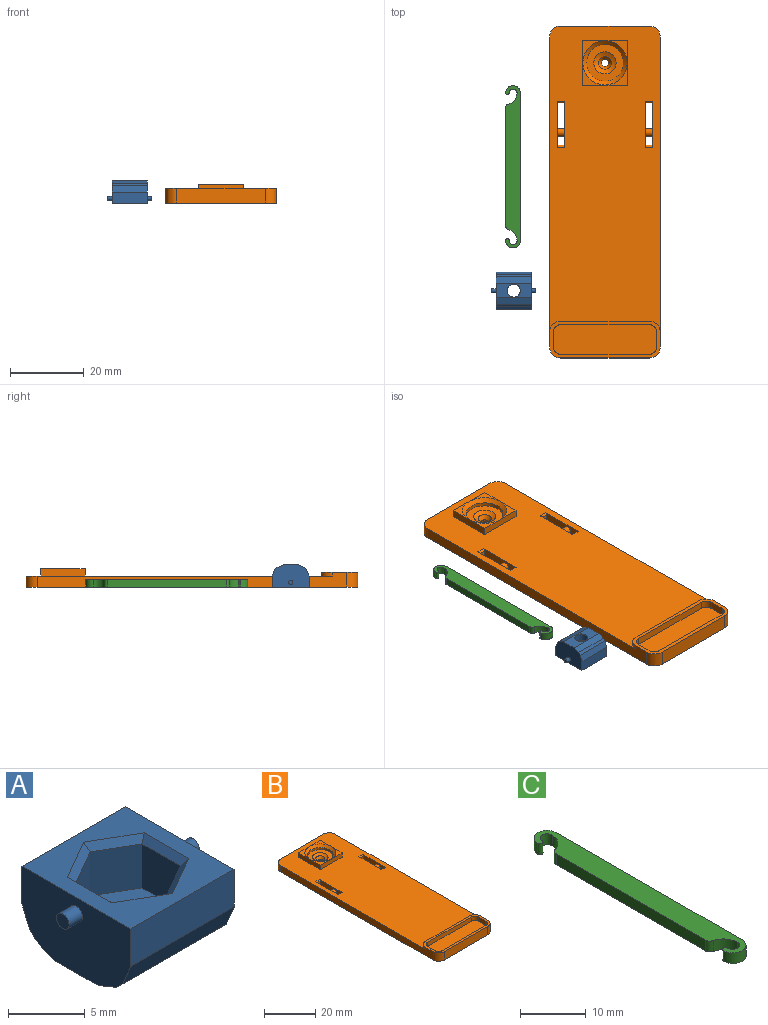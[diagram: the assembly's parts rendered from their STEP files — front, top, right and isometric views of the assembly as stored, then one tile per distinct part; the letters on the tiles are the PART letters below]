
ASSEMBLY  parts=3 mates=2
PART A: 30 faces, bbox 12x10x6 mm
  f0: plane 10x9.5mm, normal (0,0,1), area 51.6mm2, adj f3,f4,f5,f6,f24,f25,f26,f27
  f1: plane 1.15x1.15mm, normal (-1,0,0), area 1mm2, adj f2
  f2: cylinder r=0.57mm len=1.25mm, axis (1,0,0), area 4.5mm2, adj f1,f3
  f3: plane 10x6mm, normal (-1,0,0), area 53.5mm2, adj f0,f2,f4,f6,f7,f10,f11,f19
  f4: plane 9.5x3mm, normal (0,-1,0), area 28.5mm2, adj f0,f3,f5,f22
  f5: plane 10x6mm, normal (1,0,0), area 53.5mm2, adj f0,f4,f6,f7,f9,f10,f11,f19
  f6: plane 9.5x3mm, normal (0,1,0), area 28.5mm2, adj f0,f3,f5,f19
  f7: plane 9.5x4mm, normal (0,0,-1), area 28.4mm2, adj f3,f5,f20,f21,f23
  f8: plane 1.15x1.15mm, normal (1,0,0), area 1mm2, adj f9
  f9: cylinder r=0.57mm len=1.25mm, axis (1,0,0), area 4.5mm2, adj f5,f8
  f10: plane 9.5x0.59mm, normal (0,0.71,-0.71), area 7.9mm2, adj f3,f5,f19,f20
  f11: plane 9.5x0.59mm, normal (0,-0.71,-0.71), area 7.9mm2, adj f3,f5,f21,f22
  f12: plane 3.5x3.04mm, normal (-0.5,-0.87,0), area 12.3mm2, adj f13,f17,f18,f26
  f13: plane 3.5x3.04mm, normal (0.5,-0.87,0), area 12.3mm2, adj f12,f14,f18,f28
  f14: plane 3.51x3.5mm, normal (1,0,0), area 12.3mm2, adj f13,f15,f18,f29
  f15: plane 3.5x3.04mm, normal (0.5,0.87,0), area 12.3mm2, adj f14,f16,f18,f27
  f16: plane 3.5x3.04mm, normal (-0.5,0.87,0), area 12.3mm2, adj f15,f17,f18,f25
  f17: plane 3.51x3.5mm, normal (-1,0,0), area 12.3mm2, adj f12,f16,f18,f24
  f18: plane 7.02x6.08mm, normal (0,0,1), area 22.4mm2, adj f12,f13,f14,f15,f16,f17,f23
  f19: plane 9.5x1.71mm, normal (0,0.92,-0.38), area 17.6mm2, adj f3,f5,f6,f10
  f20: plane 9.5x1.71mm, normal (0,0.38,-0.92), area 17.6mm2, adj f3,f5,f7,f10
  f21: plane 9.5x1.71mm, normal (0,-0.38,-0.92), area 17.6mm2, adj f3,f5,f7,f11
  f22: plane 9.5x1.71mm, normal (0,-0.92,-0.38), area 17.6mm2, adj f3,f4,f5,f11
  f23: cylinder r=1.75mm len=3.5mm, axis (0,0,1), area 22mm2, adj f7,f18
  f24: plane 4.09x0.5mm, normal (-0.71,0,0.71), area 2.7mm2, adj f0,f17,f25,f26
  f25: plane 3.54x2.33mm, normal (-0.35,0.61,0.71), area 2.7mm2, adj f0,f16,f24,f27
  f26: plane 3.54x2.33mm, normal (-0.35,-0.61,0.71), area 2.7mm2, adj f0,f12,f24,f28
  f27: plane 3.54x2.33mm, normal (0.35,0.61,0.71), area 2.7mm2, adj f0,f15,f25,f29
  f28: plane 3.54x2.33mm, normal (0.35,-0.61,0.71), area 2.7mm2, adj f0,f13,f26,f29
  f29: plane 4.09x0.5mm, normal (0.71,0,0.71), area 2.7mm2, adj f0,f14,f27,f28
PART B: 56 faces, bbox 30x90x5 mm
  f0: plane 83x30mm, normal (0,0,1), area 2202.2mm2, adj f6,f8,f9,f12,f13,f14,f15,f16
  f1: plane 90x30mm, normal (0,0,-1), area 2631.5mm2, adj f6,f7,f8,f9,f10,f11,f12,f13
  f2: sphere r=5mm, area 21mm2, adj f32,f36
  f3: plane 6x6mm, normal (0,0,1), area 7.7mm2, adj f29,f30,f34
  f4: plane 6x6mm, normal (0,0,1), area 7.7mm2, adj f28,f29,f34
  f5: plane 6x6mm, normal (0,0,1), area 7.7mm2, adj f27,f28,f34
  f6: plane 84x4mm, normal (-1,0,0), area 256mm2, adj f0,f1,f10,f13,f16,f25
  f7: plane 24x4mm, normal (0,-1,0), area 96mm2, adj f1,f10,f11,f25
  f8: plane 84x4mm, normal (1,0,0), area 256mm2, adj f0,f1,f11,f12,f14,f25
  f9: plane 24x3mm, normal (0,1,0), area 72mm2, adj f0,f1,f12,f13
  f10: cylinder r=3mm len=4mm, axis (0,0,-1), area 18.8mm2, adj f1,f6,f7,f25
  f11: cylinder r=3mm len=4mm, axis (0,0,1), area 18.8mm2, adj f1,f7,f8,f25
  f12: cylinder r=3mm len=3mm, axis (0,0,-1), area 14.1mm2, adj f0,f1,f8,f9
  f13: cylinder r=3mm len=3mm, axis (0,0,1), area 14.1mm2, adj f0,f1,f6,f9
  f14: cylinder r=3mm len=3mm, axis (0,0,-1), area 4.7mm2, adj f0,f8,f15,f25
  f15: plane 24x1mm, normal (0,1,0), area 24mm2, adj f0,f14,f16,f25
  f16: cylinder r=3mm len=3mm, axis (0,0,-1), area 4.7mm2, adj f0,f6,f15,f25
  f17: plane 4x2mm, normal (-1,0,0), area 8mm2, adj f18,f24,f25,f26
  f18: cylinder r=2mm len=2mm, axis (0,0,-1), area 6.3mm2, adj f17,f19,f25,f26
  f19: plane 24x2mm, normal (0,1,0), area 48mm2, adj f18,f20,f25,f26
  f20: cylinder r=2mm len=2mm, axis (0,0,-1), area 6.3mm2, adj f19,f21,f25,f26
  f21: plane 4x2mm, normal (1,0,0), area 8mm2, adj f20,f22,f25,f26
  f22: cylinder r=2mm len=2mm, axis (0,0,-1), area 6.3mm2, adj f21,f23,f25,f26
  f23: plane 24x2mm, normal (0,-1,0), area 48mm2, adj f22,f24,f25,f26
  f24: cylinder r=2mm len=2mm, axis (0,0,-1), area 6.3mm2, adj f17,f23,f25,f26
  f25: plane 30x10mm, normal (0,0,1), area 71.7mm2, adj f6,f7,f8,f10,f11,f14,f15,f16
  f26: plane 28x8mm, normal (0,0,1), area 220.6mm2, adj f17,f18,f19,f20,f21,f22,f23,f24
  f27: plane 12x2mm, normal (0,1,0), area 24mm2, adj f0,f5,f28,f30,f31
  f28: plane 12x2mm, normal (-1,0,0), area 24mm2, adj f0,f4,f5,f27,f29
  f29: plane 12x2mm, normal (0,-1,0), area 24mm2, adj f0,f3,f4,f28,f30
  f30: plane 12x2mm, normal (1,0,0), area 24mm2, adj f0,f3,f27,f29,f31
  f31: plane 6x6mm, normal (0,0,1), area 7.7mm2, adj f27,f30,f34
  f32: plane 10x10mm, normal (0,0,1), area 50.3mm2, adj f2,f33
  f33: cylinder r=5mm len=10mm, axis (0,0,-1), area 31.4mm2, adj f32,f34
  f34: cone r=6mm half-angle=45deg, axis (0,0,1), area 48.9mm2, adj f3,f4,f5,f31,f33
  f35: cylinder r=1mm len=2mm, axis (0,0,1), area 4.3mm2, adj f36,f37
  f36: cone r=1.79mm half-angle=34.5deg, axis (0,0,1), area 12.2mm2, adj f2,f35
  f37: cone r=1mm half-angle=45deg, axis (0,0,-1), area 5.6mm2, adj f1,f35
  f38: plane 2.15x2mm, normal (0,-1,0), area 4.3mm2, adj f39,f40,f52,f53
  f39: plane 12.5x3mm, normal (-1,0,0), area 31.9mm2, adj f0,f1,f38,f41,f47,f52,f53,f54
  f40: plane 12.5x3mm, normal (1,0,0), area 31.9mm2, adj f0,f1,f38,f41,f47,f52,f53,f54
  f41: plane 2.15x2mm, normal (0,1,0), area 4.3mm2, adj f39,f40,f54,f55
  f42: plane 2.15x2mm, normal (0,1,0), area 4.3mm2, adj f43,f45,f49,f50
  f43: plane 12.5x3mm, normal (-1,0,0), area 31.9mm2, adj f0,f1,f42,f44,f46,f48,f49,f50
  f44: plane 2.15x2mm, normal (0,-1,0), area 4.3mm2, adj f43,f45,f48,f51
  f45: plane 12.5x3mm, normal (1,0,0), area 31.9mm2, adj f0,f1,f42,f44,f46,f48,f49,f50
  f46: cylinder r=1mm len=2.15mm, axis (-1,0,0), area 13.5mm2, adj f43,f45
  f47: cylinder r=1mm len=2.15mm, axis (-1,0,0), area 13.5mm2, adj f39,f40
  f48: plane 2.15x0.5mm, normal (0,-0.71,0.71), area 1.5mm2, adj f0,f43,f44,f45
  f49: plane 2.15x0.5mm, normal (0,0.71,0.71), area 1.5mm2, adj f0,f42,f43,f45
  f50: plane 2.15x0.5mm, normal (0,0.71,-0.71), area 1.5mm2, adj f1,f42,f43,f45
  f51: plane 2.15x0.5mm, normal (0,-0.71,-0.71), area 1.5mm2, adj f1,f43,f44,f45
  f52: plane 2.15x0.5mm, normal (0,-0.71,-0.71), area 1.5mm2, adj f1,f38,f39,f40
  f53: plane 2.15x0.5mm, normal (0,-0.71,0.71), area 1.5mm2, adj f0,f38,f39,f40
  f54: plane 2.15x0.5mm, normal (0,0.71,-0.71), area 1.5mm2, adj f1,f39,f40,f41
  f55: plane 2.15x0.5mm, normal (0,0.71,0.71), area 1.5mm2, adj f0,f39,f40,f41
PART C: 14 faces, bbox 4x44x2 mm
  f0: cylinder r=1.07mm len=2.15mm, axis (0,0,-1), area 6.8mm2, adj f1,f9,f10,f11
  f1: cylinder r=3.08mm len=2.98mm, axis (0,0,-1), area 8.1mm2, adj f0,f10,f11,f12
  f2: plane 32.1x2mm, normal (-1,0,0), area 64.2mm2, adj f10,f11,f12,f13
  f3: cylinder r=3.08mm len=2.98mm, axis (0,0,-1), area 8.1mm2, adj f4,f10,f11,f13
  f4: cylinder r=1.07mm len=2.15mm, axis (0,0,-1), area 6.8mm2, adj f3,f5,f10,f11
  f5: cylinder r=0.46mm len=2mm, axis (0,0,-1), area 2.9mm2, adj f4,f6,f10,f11
  f6: cylinder r=2mm len=4mm, axis (0,0,-1), area 12.6mm2, adj f5,f7,f10,f11
  f7: plane 40x2mm, normal (1,0,0), area 80mm2, adj f6,f8,f10,f11
  f8: cylinder r=2mm len=4mm, axis (0,0,-1), area 12.6mm2, adj f7,f9,f10,f11
  f9: cylinder r=0.46mm len=2mm, axis (0,0,-1), area 2.9mm2, adj f0,f8,f10,f11
  f10: plane 44x4mm, normal (0,0,1), area 154.5mm2, adj f0,f1,f2,f3,f4,f5,f6,f7
  f11: plane 44x4mm, normal (0,0,-1), area 154.5mm2, adj f0,f1,f2,f3,f4,f5,f6,f7
  f12: cylinder r=1mm len=2mm, axis (0,0,-1), area 2.6mm2, adj f1,f2,f10,f11
  f13: cylinder r=1mm len=2mm, axis (0,0,-1), area 2.6mm2, adj f2,f3,f10,f11
PLACE A rot(axis=(1,0,0),180deg) t=(-64.71,17.21,18)mm
PLACE B at identity fixed
PLACE C t=(6.74,-17.45,0)mm
MATE planar A.f0 <-> B.f1  axis (0,0,-1) through (-29.34,-25.34,0)mm
MATE planar B.f1 <-> C.f12  axis (0,0,-1) through (-17.85,4.47,0)mm
